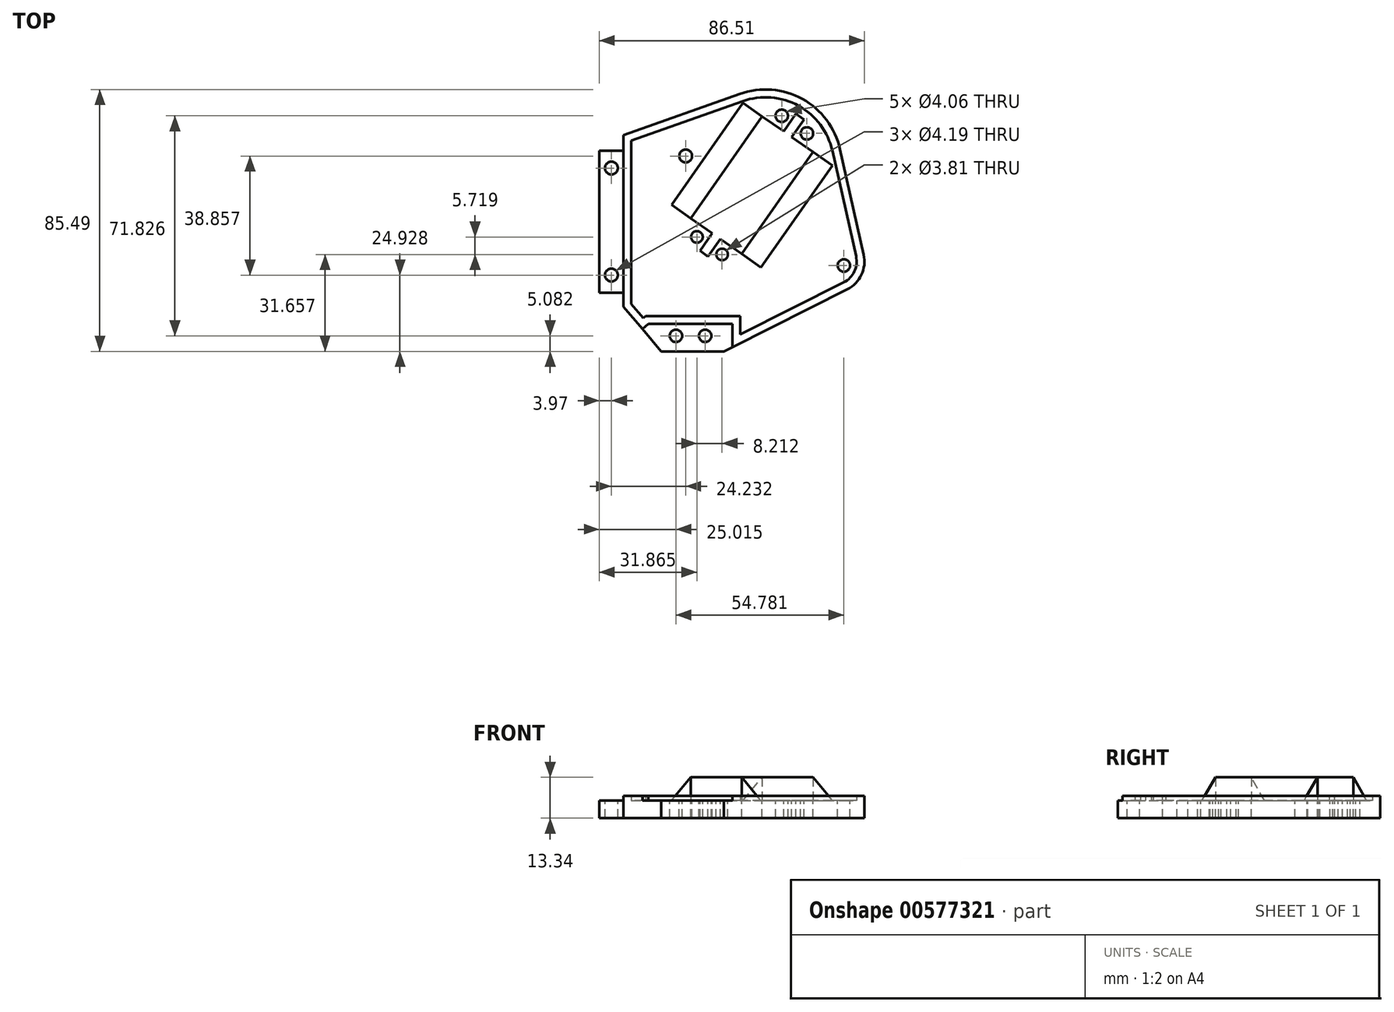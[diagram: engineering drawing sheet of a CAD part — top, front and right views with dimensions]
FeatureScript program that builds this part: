
annotation { "Feature Type Name" : "Feature", "Feature Type Description" : "" }
export const myFeature = defineFeature(function(context is Context, id is Id, definition is map)
    precondition{}
    {
        {
            var Q0;
            Q0=qCreatedBy(makeId("Top.planeOp"),FACE);
            var sketch = newSketch(context, id + "F0", { "sketchPlane" : qUnion([Q0])});
            skArc(sketch, "E0", {"start": v(35.25, 23.23) * mm, "mid": v(23, 39.59) * mm, "end": v(2.62, 41.27) * mm});
            skArc(sketch, "E1", {"start": v(37.63, -22.5) * mm, "mid": v(42.25, -17.77) * mm, "end": v(42.98, -11.2) * mm});
            skLineSegment(sketch, "E2", {"start": v(-35.34, 27.86) * mm, "end": v(2.62, 41.27) * mm});
            skLineSegment(sketch, "E3", {"start": v(42.98, -11.2) * mm, "end": v(35.25, 23.23) * mm});
            skLineSegment(sketch, "E4", {"start": v(-2.65, -42.79) * mm, "end": v(37.63, -22.5) * mm});
            skLineSegment(sketch, "E5", {"start": v(-2.65, -42.79) * mm, "end": v(-23.08, -42.79) * mm});
            skLineSegment(sketch, "E6", {"start": v(-23.08, -42.79) * mm, "end": v(-35.34, -28.2) * mm});
            skLineSegment(sketch, "E7", {"start": v(-35.34, -28.2) * mm, "end": v(-35.34, -23.58) * mm});
            skLineSegment(sketch, "E8", {"start": v(-35.34, -23.58) * mm, "end": v(-43.28, -23.58) * mm});
            skLineSegment(sketch, "E9", {"start": v(-43.28, -23.58) * mm, "end": v(-43.28, 22.78) * mm});
            skLineSegment(sketch, "E10", {"start": v(-43.28, 22.78) * mm, "end": v(-35.34, 22.78) * mm});
            skLineSegment(sketch, "E11", {"start": v(-35.34, 22.78) * mm, "end": v(-35.34, 27.86) * mm});
            skLineSegment(sketch, "E12.bottom", {"start": v(3.2, -11) * mm, "end": v(26.5, 22.3) * mm});
            skLineSegment(sketch, "E12.top", {"start": v(-13.45, 0.66) * mm, "end": v(9.86, 33.96) * mm});
            skLineSegment(sketch, "E12.left", {"start": v(3.2, -11) * mm, "end": v(-13.45, 0.66) * mm});
            skLineSegment(sketch, "E12.right", {"start": v(26.5, 22.3) * mm, "end": v(9.86, 33.96) * mm});
            skLineSegment(sketch, "E13.bottom", {"start": v(19.48, 27.22) * mm, "end": v(23.49, 32.94) * mm});
            skLineSegment(sketch, "E13.top", {"start": v(16.88, 29.04) * mm, "end": v(20.89, 34.76) * mm});
            skLineSegment(sketch, "E13.right", {"start": v(23.49, 32.94) * mm, "end": v(20.89, 34.76) * mm});
            skLineSegment(sketch, "E14", {"start": v(-6.43, -4.25) * mm, "end": v(-10.44, -9.97) * mm});
            skLineSegment(sketch, "E15", {"start": v(-10.44, -9.97) * mm, "end": v(-7.84, -11.8) * mm});
            skLineSegment(sketch, "E16", {"start": v(-7.84, -11.8) * mm, "end": v(-3.83, -6.07) * mm});
            skLineSegment(sketch, "E17", {"start": v(-5.13, -5.16) * mm, "end": v(18.18, 28.13) * mm, "construction": true});
            skCircle(sketch, "E18", {"center": v(-39.3, 17.06) * mm, "radius": 2.1 * mm});
            skLineSegment(sketch, "E19", {"start": v(-39.3, 22.78) * mm, "end": v(-39.3, -23.58) * mm, "construction": true});
            skCircle(sketch, "E20", {"center": v(-39.3, -17.86) * mm, "radius": 2.1 * mm});
            skCircle(sketch, "E21", {"center": v(16.27, 34.12) * mm, "radius": 2.03 * mm});
            skCircle(sketch, "E22", {"center": v(24.46, 28.38) * mm, "radius": 2.03 * mm});
            skCircle(sketch, "E23", {"center": v(-3.2, -11.13) * mm, "radius": 1.9 * mm});
            skCircle(sketch, "E24", {"center": v(-11.41, -5.41) * mm, "radius": 1.9 * mm});
            skCircle(sketch, "E25", {"center": v(36.52, -14.73) * mm, "radius": 2.03 * mm});
            skCircle(sketch, "E26", {"center": v(-18.26, -37.7) * mm, "radius": 2.03 * mm});
            skCircle(sketch, "E27", {"center": v(-8.74, -37.7) * mm, "radius": 2.03 * mm});
            skCircle(sketch, "E28", {"center": v(-15.08, 21) * mm, "radius": 2.1 * mm});
            skSolve(sketch);
        }
        {
            var Q0;
            Q0=makeQuery(id+"F0.imprint","IMPRINT",FACE,{"disambiguationData":[TD([[makeQuery(id+"F0.imprint","IMPRINT",EDGE,{"derivedFrom":sQuery(id+"F0.wireOp",EDGE,"E0")}),1.0]])]});
            extrude(context, id + "F1", {"entities" : qUnion([Q0]), "oppositeDirection" : true, "depth" : 5.7 * mm, "offsetDistance" : 25.4 * mm});
        }
        {
            var Q0;
            Q0=makeQuery(id+"F1.opExtrude","CAP_FACE",FACE,{"disambiguationData":[OSD([sQuery(id+"F0.wireOp",EDGE,"E0"),sQuery(id+"F0.wireOp",EDGE,"E1"),sQuery(id+"F0.wireOp",EDGE,"E2"),sQuery(id+"F0.wireOp",EDGE,"E3"),sQuery(id+"F0.wireOp",EDGE,"E4"),sQuery(id+"F0.wireOp",EDGE,"E5"),sQuery(id+"F0.wireOp",EDGE,"E6"),sQuery(id+"F0.wireOp",EDGE,"E7"),sQuery(id+"F0.wireOp",EDGE,"E8"),sQuery(id+"F0.wireOp",EDGE,"E9"),sQuery(id+"F0.wireOp",EDGE,"E10"),sQuery(id+"F0.wireOp",EDGE,"E11"),sQuery(id+"F0.wireOp",EDGE,"E12.bottom"),sQuery(id+"F0.wireOp",EDGE,"E12.top"),sQuery(id+"F0.wireOp",EDGE,"E12.left"),sQuery(id+"F0.wireOp",EDGE,"E12.right"),sQuery(id+"F0.wireOp",EDGE,"E13.bottom"),sQuery(id+"F0.wireOp",EDGE,"E13.top"),sQuery(id+"F0.wireOp",EDGE,"E13.right"),sQuery(id+"F0.wireOp",EDGE,"E14"),sQuery(id+"F0.wireOp",EDGE,"E15"),sQuery(id+"F0.wireOp",EDGE,"E16"),sQuery(id+"F0.wireOp",EDGE,"E18"),sQuery(id+"F0.wireOp",EDGE,"E20"),sQuery(id+"F0.wireOp",EDGE,"E21"),sQuery(id+"F0.wireOp",EDGE,"E22"),sQuery(id+"F0.wireOp",EDGE,"E23"),sQuery(id+"F0.wireOp",EDGE,"E24"),sQuery(id+"F0.wireOp",EDGE,"E25"),sQuery(id+"F0.wireOp",EDGE,"E26"),sQuery(id+"F0.wireOp",EDGE,"E27"),sQuery(id+"F0.wireOp",EDGE,"E28")])],"isStart":true});
            var sketch = newSketch(context, id + "F2", { "sketchPlane" : qUnion([Q0])});
            skLineSegment(sketch, "E29.0.3", {"start": v(-35.34, -23.58) * mm, "end": v(-35.34, -28.2) * mm});
            skLineSegment(sketch, "E29.0.4", {"start": v(-35.34, -28.2) * mm, "end": v(-29.21, -35.49) * mm});
            skLineSegment(sketch, "E29.0.6", {"start": v(0.19, -41.36) * mm, "end": v(37.63, -22.5) * mm});
            skArc(sketch, "E29.0.7", {"start": v(37.63, -22.5) * mm, "mid": v(42.25, -17.77) * mm, "end": v(42.98, -11.2) * mm});
            skLineSegment(sketch, "E29.0.8", {"start": v(42.98, -11.2) * mm, "end": v(35.25, 23.23) * mm});
            skArc(sketch, "E29.0.9", {"start": v(35.25, 23.23) * mm, "mid": v(23, 39.59) * mm, "end": v(2.62, 41.27) * mm});
            skLineSegment(sketch, "E29.0.10", {"start": v(2.62, 41.27) * mm, "end": v(-35.34, 27.86) * mm});
            skLineSegment(sketch, "E29.0.11", {"start": v(-35.34, 27.86) * mm, "end": v(-35.34, 22.78) * mm});
            skLineSegment(sketch, "E30", {"start": v(-35.34, -23.58) * mm, "end": v(-35.34, 22.78) * mm});
            skLineSegment(sketch, "E31.0", {"start": v(3.46, 38.88) * mm, "end": v(-32.8, 26.06) * mm});
            skArc(sketch, "E31.1", {"start": v(32.77, 22.67) * mm, "mid": v(21.76, 37.36) * mm, "end": v(3.46, 38.88) * mm});
            skLineSegment(sketch, "E31.2", {"start": v(-32.8, 26.06) * mm, "end": v(-32.8, 22.78) * mm});
            skLineSegment(sketch, "E31.3", {"start": v(40.5, -11.75) * mm, "end": v(32.77, 22.67) * mm});
            skArc(sketch, "E31.4", {"start": v(36.49, -20.23) * mm, "mid": v(39.95, -16.68) * mm, "end": v(40.5, -11.75) * mm});
            skLineSegment(sketch, "E31.5", {"start": v(0.19, -38.52) * mm, "end": v(36.49, -20.23) * mm});
            skLineSegment(sketch, "E31.6", {"start": v(-32.8, -23.58) * mm, "end": v(-32.8, 22.78) * mm});
            skLineSegment(sketch, "E31.7", {"start": v(-32.8, -23.58) * mm, "end": v(-32.8, -27.27) * mm});
            skLineSegment(sketch, "E31.8", {"start": v(-32.8, -27.27) * mm, "end": v(-27.27, -33.86) * mm});
            skLineSegment(sketch, "E32", {"start": v(-29.21, -35.49) * mm, "end": v(-27.27, -33.86) * mm});
            skLineSegment(sketch, "E33", {"start": v(0.19, -41.36) * mm, "end": v(0.19, -38.52) * mm});
            skPoint(sketch, "E29.0.5.start.orphan", {"position": v(-23.08, -42.79) * mm});
            skPoint(sketch, "E34.orphan", {"position": v(-2.65, -42.79) * mm});
            skPoint(sketch, "E29.0.0.end.orphan", {"position": v(-43.28, 22.78) * mm});
            skPoint(sketch, "E29.0.2.start.orphan", {"position": v(-43.28, -23.58) * mm});
            skSolve(sketch);
        }
        {
            var Q0;
            Q0 = qSketchRegion(id + "F2", true);
            extrude(context, id + "F3", {"entities" : qUnion([Q0]), "operationType" : NewBodyOperationType.ADD, "depth" : 1.52 * mm, "offsetDistance" : 25.4 * mm});
        }
        {
            var Q0;
            {var subQ0=sQuery(id+"F0.wireOp",EDGE,"E27");var subQ1=sQuery(id+"F0.wireOp",EDGE,"E26");var subQ2=sQuery(id+"F0.wireOp",EDGE,"E25");var subQ3=sQuery(id+"F0.wireOp",EDGE,"E21");var subQ4=sQuery(id+"F0.wireOp",EDGE,"E16");var subQ5=sQuery(id+"F0.wireOp",EDGE,"E15");var subQ6=sQuery(id+"F0.wireOp",EDGE,"E14");var subQ7=sQuery(id+"F0.wireOp",EDGE,"E13.right");var subQ8=sQuery(id+"F0.wireOp",EDGE,"E13.top");var subQ9=sQuery(id+"F0.wireOp",EDGE,"E12.bottom");var subQ10=sQuery(id+"F0.wireOp",EDGE,"E24");var subQ11=sQuery(id+"F0.wireOp",EDGE,"E6");var subQ12=sQuery(id+"F0.wireOp",EDGE,"E12.right");var subQ13=sQuery(id+"F0.wireOp",EDGE,"E12.top");var subQ14=sQuery(id+"F0.wireOp",EDGE,"E23");var subQ15=sQuery(id+"F0.wireOp",EDGE,"E5");var subQ16=sQuery(id+"F0.wireOp",EDGE,"E13.bottom");var subQ17=sQuery(id+"F0.wireOp",EDGE,"E22");var subQ18=sQuery(id+"F0.wireOp",EDGE,"E4");var subQ19=sQuery(id+"F0.wireOp",EDGE,"E12.left");var subQ20=sQuery(id+"F0.wireOp",EDGE,"E28");Q0=makeQuery(id+"F3.boolean.opBoolean","SPLIT",FACE,{"disambiguationData":[TD([makeQuery(id+"F1.opExtrude","SWEPT_FACE",FACE,{"disambiguationData":[OSD([subQ18])]})])],"derivedFrom":makeQuery(id+"F1.opExtrude","CAP_FACE",FACE,{"disambiguationData":[OSD([sQuery(id+"F0.wireOp",EDGE,"E0"),sQuery(id+"F0.wireOp",EDGE,"E1"),sQuery(id+"F0.wireOp",EDGE,"E2"),sQuery(id+"F0.wireOp",EDGE,"E3"),subQ18,subQ15,subQ11,sQuery(id+"F0.wireOp",EDGE,"E7"),sQuery(id+"F0.wireOp",EDGE,"E8"),sQuery(id+"F0.wireOp",EDGE,"E9"),sQuery(id+"F0.wireOp",EDGE,"E10"),sQuery(id+"F0.wireOp",EDGE,"E11"),subQ9,subQ13,subQ19,subQ12,subQ16,subQ8,subQ7,subQ6,subQ5,subQ4,sQuery(id+"F0.wireOp",EDGE,"E18"),sQuery(id+"F0.wireOp",EDGE,"E20"),subQ3,subQ17,subQ14,subQ10,subQ2,subQ1,subQ0,subQ20])],"isStart":true})});}
            var sketch = newSketch(context, id + "F4", { "sketchPlane" : qUnion([Q0])});
            skLineSegment(sketch, "E35", {"start": v(-27.27, -33.86) * mm, "end": v(0.19, -33.86) * mm});
            skLineSegment(sketch, "E36", {"start": v(0.19, -33.86) * mm, "end": v(0.19, -38.52) * mm});
            skLineSegment(sketch, "E37", {"start": v(2.73, -37.24) * mm, "end": v(2.73, -31.32) * mm});
            skLineSegment(sketch, "E38", {"start": v(2.73, -31.32) * mm, "end": v(-28.2, -31.32) * mm});
            skLineSegment(sketch, "E39", {"start": v(-28.2, -31.32) * mm, "end": v(-28.9, -31.91) * mm});
            skLineSegment(sketch, "E40", {"start": v(-28.9, -31.91) * mm, "end": v(-27.27, -33.86) * mm});
            skLineSegment(sketch, "E41", {"start": v(0.19, -38.52) * mm, "end": v(2.73, -37.24) * mm});
            skSolve(sketch);
        }
        {
            var Q0;
            Q0 = qSketchRegion(id + "F4", true);
            extrude(context, id + "F5", {"entities" : qUnion([Q0]), "operationType" : NewBodyOperationType.ADD, "depth" : 1.52 * mm, "offsetDistance" : 25.4 * mm});
        }
        {
            var Q0;
            {var subQ0=sQuery(id+"F0.wireOp",EDGE,"E12.right");Q0=makeQuery(id+"F1.opExtrude","SWEPT_FACE",FACE,{"disambiguationData":[OSD([subQ0]),TDD([makeQuery(id+"F0.imprint","IMPRINT",EDGE,{"disambiguationData":[TD([[makeQuery(id+"F0.imprint","INTERSECT",VERTEX,{"derivedFrom":[sQuery(id+"F0.wireOp",EDGE,"E12.top"),subQ0]}),1.0]])],"derivedFrom":subQ0})])]});}
            var sketch = newSketch(context, id + "F6", { "sketchPlane" : qUnion([Q0])});
            skLineSegment(sketch, "E42", {"start": v(-11.4, 0) * mm, "end": v(-19.02, 0) * mm});
            skLineSegment(sketch, "E43", {"start": v(-19.02, 0) * mm, "end": v(-11.4, 7.62) * mm});
            skLineSegment(sketch, "E44", {"start": v(-11.4, 7.62) * mm, "end": v(-11.4, 0) * mm});
            skPoint(sketch, "E45.0", {"position": v(8.92, 0) * mm});
            skLineSegment(sketch, "E46", {"start": v(8.92, 0) * mm, "end": v(16.54, 0) * mm});
            skLineSegment(sketch, "E47", {"start": v(16.54, 0) * mm, "end": v(8.92, 7.62) * mm});
            skLineSegment(sketch, "E48", {"start": v(8.92, 7.62) * mm, "end": v(8.92, 0) * mm});
            skSolve(sketch);
        }
        {
            var Q0;
            Q0=makeQuery(id+"F6.imprint","IMPRINT",FACE,{"disambiguationData":[TD([[makeQuery(id+"F6.imprint","IMPRINT",EDGE,{"derivedFrom":sQuery(id+"F6.wireOp",EDGE,"E42")}),-1.0]])]});
            var Q1;
            Q1=makeQuery(id+"F6.imprint","IMPRINT",FACE,{"disambiguationData":[TD([[makeQuery(id+"F6.imprint","IMPRINT",EDGE,{"derivedFrom":sQuery(id+"F6.wireOp",EDGE,"E46")}),1.0]])]});
            extrude(context, id + "F7", {"entities" : qUnion([Q0, Q1]), "operationType" : NewBodyOperationType.ADD, "depth" : 40.64 * mm, "offsetDistance" : 25.4 * mm});
        }
    });
